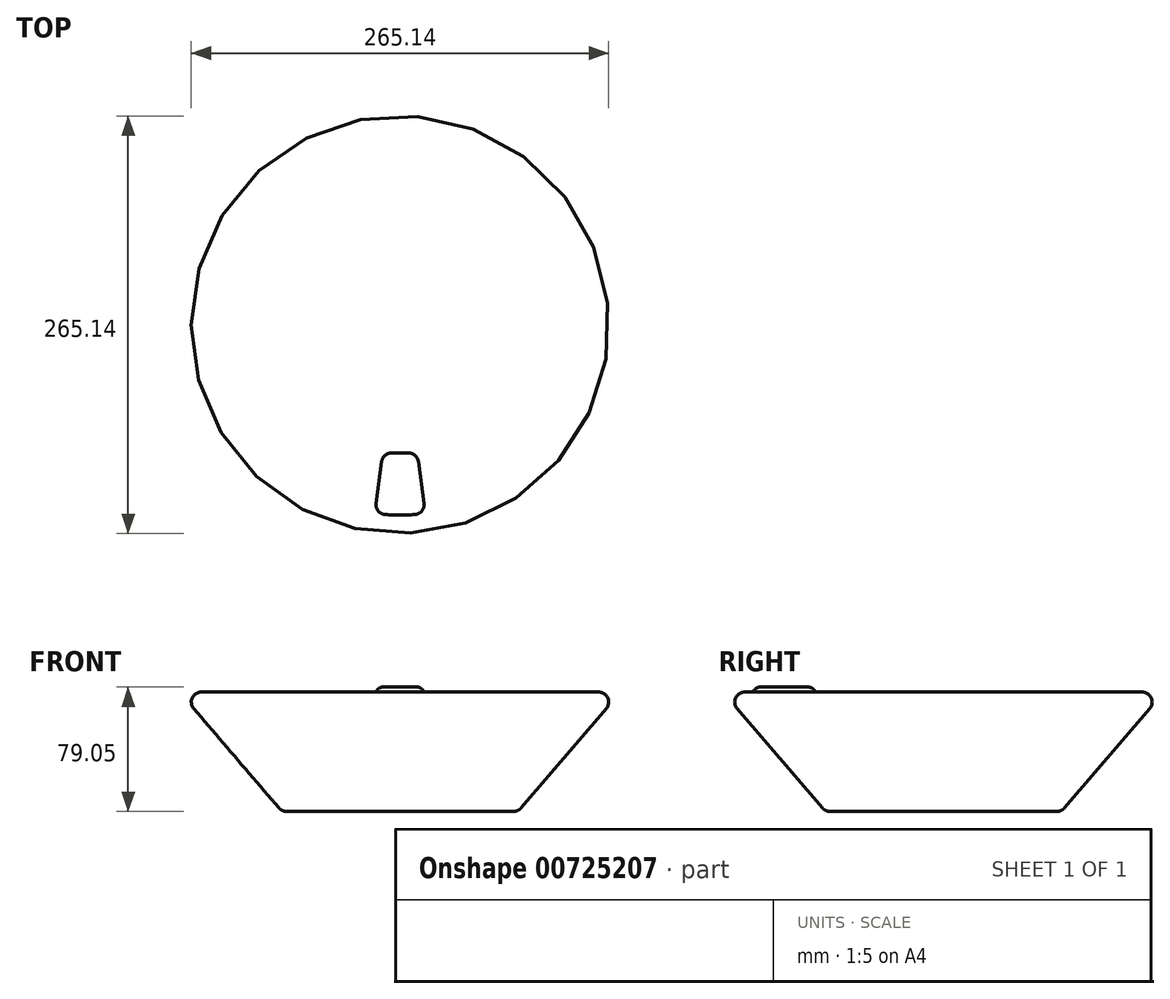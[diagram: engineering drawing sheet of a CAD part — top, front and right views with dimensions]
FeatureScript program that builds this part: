
annotation { "Feature Type Name" : "Feature", "Feature Type Description" : "" }
export const myFeature = defineFeature(function(context is Context, id is Id, definition is map)
    precondition{}
    {
        {
            var Q0;
            Q0=qCreatedBy(makeId("Front.planeOp"),FACE);
            var sketch = newSketch(context, id + "F0", { "sketchPlane" : qUnion([Q0])});
            skLineSegment(sketch, "E0", {"start": v(0, 0) * mm, "end": v(0, 0) * mm});
            skLineSegment(sketch, "E1", {"start": v(0, 0) * mm, "end": v(0, -75.88) * mm});
            skLineSegment(sketch, "E2", {"start": v(0, -75.88) * mm, "end": v(72.11, -75.88) * mm});
            skLineSegment(sketch, "E3", {"start": v(0, 0) * mm, "end": v(126.22, 0) * mm});
            skLineSegment(sketch, "E4", {"start": v(131.04, -10.48) * mm, "end": v(76.94, -73.66) * mm});
            skPoint(sketch, "E5.visualSharp", {"position": v(140.02, 0) * mm});
            skArc(sketch, "E5.filletArc", {"start": v(131.04, -10.48) * mm, "mid": v(131.99, -3.7) * mm, "end": v(126.22, 0) * mm});
            skPoint(sketch, "E6.visualSharp", {"position": v(75.03, -75.88) * mm});
            skArc(sketch, "E6.filletArc", {"start": v(72.11, -75.88) * mm, "mid": v(74.77, -75.3) * mm, "end": v(76.94, -73.66) * mm});
            skSolve(sketch);
        }
        {
            var Q0;
            Q0=makeQuery(id+"F0.imprint","IMPRINT",FACE,{"disambiguationData":[TD([[makeQuery(id+"F0.imprint","IMPRINT",EDGE,{"derivedFrom":sQuery(id+"F0.wireOp",EDGE,"E1")}),1.0]])]});
            var Q1;
            Q1=sQuery(id+"F0.wireOp",EDGE,"E1");
            revolve(context, id + "F1", {"surfaceOperationType" : NewSurfaceOperationType.ADD, "entities" : qUnion([Q0]), "axis" : qUnion([Q1]), "revolveType" : RevolveType.FULL, "oppositeDirection" : true});
        }
        {
            var Q0;
            Q0=makeQuery(id+"F1.opRevolve","SWEPT_FACE",FACE,{"disambiguationData":[OSD([sQuery(id+"F0.wireOp",EDGE,"E3")])]});
            var sketch = newSketch(context, id + "F2", { "sketchPlane" : qUnion([Q0])});
            skLineSegment(sketch, "E7", {"start": v(11.67, -86.89) * mm, "end": v(15.23, -113.37) * mm});
            skLineSegment(sketch, "E8.MirrorCS", {"start": v(-11.67, -86.89) * mm, "end": v(-15.23, -113.37) * mm});
            skArc(sketch, "E9", {"start": v(9.43, -120.54) * mm, "mid": v(0, -120.91) * mm, "end": v(-9.43, -120.54) * mm});
            skLineSegment(sketch, "E10", {"start": v(5.38, -81.38) * mm, "end": v(-5.38, -81.38) * mm});
            skPoint(sketch, "E11.visualSharp", {"position": v(10.93, -81.38) * mm});
            skArc(sketch, "E11.filletArc", {"start": v(11.67, -86.89) * mm, "mid": v(9.56, -82.95) * mm, "end": v(5.38, -81.38) * mm});
            skPoint(sketch, "E12.visualSharp", {"position": v(-10.93, -81.38) * mm});
            skArc(sketch, "E12.filletArc", {"start": v(-5.38, -81.38) * mm, "mid": v(-9.56, -82.95) * mm, "end": v(-11.67, -86.89) * mm});
            skPoint(sketch, "E13.visualSharp", {"position": v(16.1, -119.83) * mm});
            skArc(sketch, "E13.filletArc", {"start": v(9.43, -120.54) * mm, "mid": v(13.87, -118.2) * mm, "end": v(15.23, -113.37) * mm});
            skPoint(sketch, "E14.visualSharp", {"position": v(-16.1, -119.83) * mm});
            skArc(sketch, "E14.filletArc", {"start": v(-15.23, -113.37) * mm, "mid": v(-13.87, -118.2) * mm, "end": v(-9.43, -120.54) * mm});
            skLineSegment(sketch, "E15", {"start": v(0, 0) * mm, "end": v(0, -81.38) * mm});
            skSolve(sketch);
        }
        {
            var Q0;
            Q0 = qSketchRegion(id + "F2", true);
            extrude(context, id + "F3", {"entities" : qUnion([Q0]), "operationType" : NewBodyOperationType.ADD, "depth" : 3.17 * mm, "offsetDistance" : 25.4 * mm});
        }
        {
            var Q0;
            Q0=makeQuery(id+"F3.opExtrude","CAP_EDGE",EDGE,{"disambiguationData":[OSD([sQuery(id+"F2.wireOp",EDGE,"E7")])],"isStart":false});
            fillet(context, id + "F4", {"entities" : qUnion([Q0]), "radius" : 5.08 * mm, "tangentPropagation" : true, "allowEdgeOverflow" : false});
        }
    });
